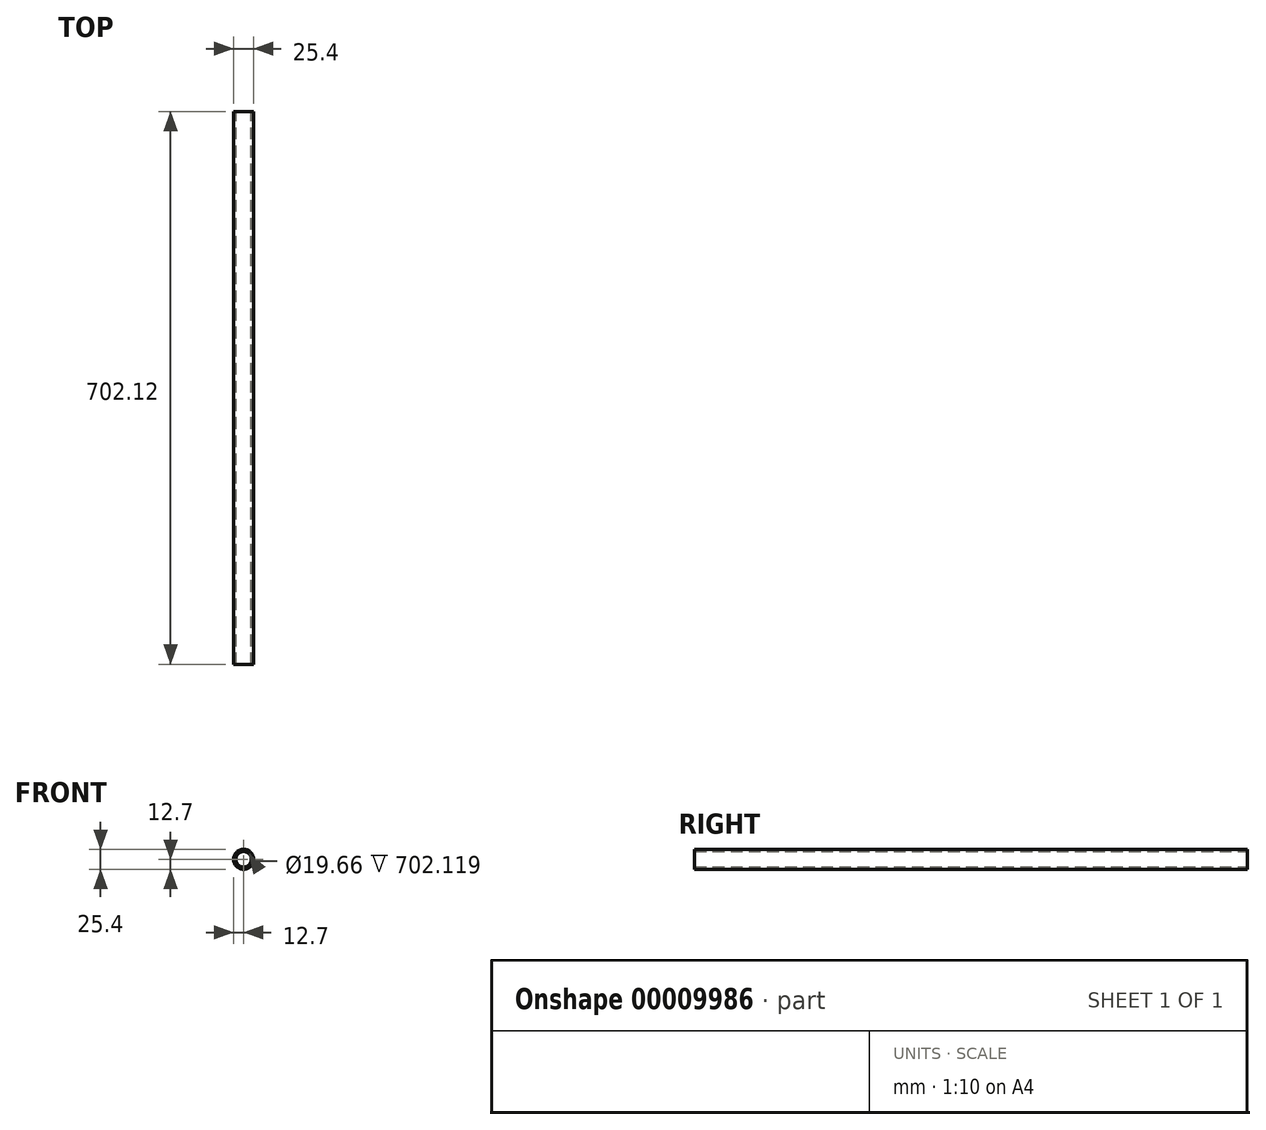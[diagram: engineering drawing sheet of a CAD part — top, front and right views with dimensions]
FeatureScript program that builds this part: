
annotation { "Feature Type Name" : "Feature", "Feature Type Description" : "" }
export const myFeature = defineFeature(function(context is Context, id is Id, definition is map)
    precondition{}
    {
        {
            var Q0;
            Q0=qCreatedBy(makeId("Front.planeOp"),FACE);
            var sketch = newSketch(context, id + "F0", { "sketchPlane" : qUnion([Q0])});
            skCircle(sketch, "E0", {"center": v(0, 0) * mm, "radius": 12.7 * mm});
            skCircle(sketch, "E1", {"center": v(0, 0) * mm, "radius": 9.83 * mm});
            skSolve(sketch);
        }
        {
            var Q0;
            Q0 = qSketchRegion(id + "F0", true);
            extrude(context, id + "F1", {"entities" : qUnion([Q0]), "depth" : 812.8 * mm - 100.75 * mm - 9.93 * mm});
        }
    });
